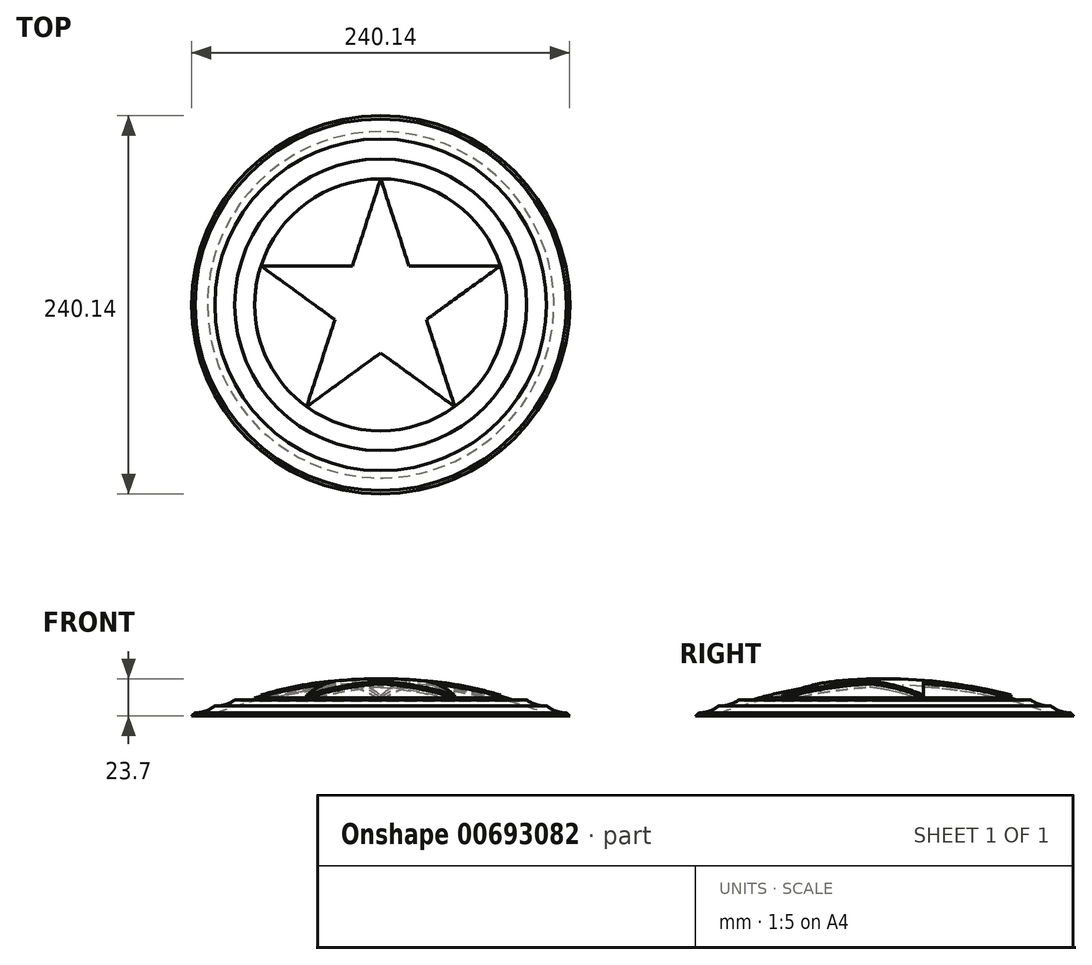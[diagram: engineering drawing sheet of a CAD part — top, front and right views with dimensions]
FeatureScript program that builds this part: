
annotation { "Feature Type Name" : "Feature", "Feature Type Description" : "" }
export const myFeature = defineFeature(function(context is Context, id is Id, definition is map)
    precondition{}
    {
        {
            var Q0;
            Q0=qCreatedBy(makeId("Front.planeOp"),FACE);
            var sketch = newSketch(context, id + "F0", { "sketchPlane" : qUnion([Q0])});
            skPoint(sketch, "E0", {"position": v(0, 111.23) * mm});
            skLineSegment(sketch, "E1", {"start": v(0, 111.23) * mm, "end": v(0, 131.23) * mm});
            skPoint(sketch, "E2.orphan", {"position": v(-118, 111.23) * mm});
            skPoint(sketch, "E3", {"position": v(0, -180.77) * mm});
            skPoint(sketch, "E4", {"position": v(118, 141.23) * mm});
            skPoint(sketch, "E5", {"position": v(0, 141.23) * mm});
            skLineSegment(sketch, "E6", {"start": v(118, 141.23) * mm, "end": v(105.33, 141.23) * mm, "construction": true});
            skLineSegment(sketch, "E7", {"start": v(105.33, 141.23) * mm, "end": v(92.67, 141.23) * mm, "construction": true});
            skLineSegment(sketch, "E8", {"start": v(92.67, 141.23) * mm, "end": v(80, 141.23) * mm, "construction": true});
            skLineSegment(sketch, "E9", {"start": v(80, 141.23) * mm, "end": v(0, 141.23) * mm, "construction": true});
            skPoint(sketch, "E10", {"position": v(80, 120.8) * mm});
            skPoint(sketch, "E11", {"position": v(92.67, 119.52) * mm});
            skPoint(sketch, "E12", {"position": v(105.33, 141.23) * mm});
            skPoint(sketch, "E13", {"position": v(105.33, 115.67) * mm});
            skArc(sketch, "E14", {"start": v(80, 120.8) * mm, "mid": v(86.23, 119.14) * mm, "end": v(92.67, 119.52) * mm});
            skPoint(sketch, "E15", {"position": v(86.23, 119.14) * mm});
            skArc(sketch, "E16", {"start": v(92.67, 119.52) * mm, "mid": v(98.68, 116.53) * mm, "end": v(105.33, 115.67) * mm});
            skArc(sketch, "E17", {"start": v(105.33, 115.67) * mm, "mid": v(111.29, 112.37) * mm, "end": v(118, 111.23) * mm});
            skPoint(sketch, "E18", {"position": v(98.68, 116.53) * mm});
            skPoint(sketch, "E19", {"position": v(111.29, 112.37) * mm});
            skLineSegment(sketch, "E20", {"start": v(86.23, 119.14) * mm, "end": v(88.27, 139.32) * mm, "construction": true});
            skLineSegment(sketch, "E21", {"start": v(98.68, 116.53) * mm, "end": v(104.57, 135.94) * mm, "construction": true});
            skLineSegment(sketch, "E22", {"start": v(111.29, 112.37) * mm, "end": v(118, 131.52) * mm, "construction": true});
            skArc(sketch, "E23", {"start": v(118, 111.23) * mm, "mid": v(119.12, 110.32) * mm, "end": v(120.07, 109.23) * mm});
            skLineSegment(sketch, "E24", {"start": v(120.07, 109.23) * mm, "end": v(0, 109.23) * mm});
            skLineSegment(sketch, "E25", {"start": v(0, 111.23) * mm, "end": v(0, 109.23) * mm});
            skArc(sketch, "E26.trimOffspring", {"start": v(80, 120.8) * mm, "mid": v(40.34, 128.61) * mm, "end": v(0, 131.23) * mm});
            skSolve(sketch);
        }
        {
            var Q0;
            Q0=makeQuery(id+"F0.imprint","IMPRINT",FACE,{"disambiguationData":[TD([[makeQuery(id+"F0.imprint","IMPRINT",EDGE,{"derivedFrom":sQuery(id+"F0.wireOp",EDGE,"E1")}),-1.0]])]});
            var Q1;
            Q1=sQuery(id+"F0.wireOp",EDGE,"E1");
            revolve(context, id + "F1", {"entities" : qUnion([Q0]), "axis" : qUnion([Q1]), "revolveType" : RevolveType.FULL});
        }
        {
            var Q0;
            Q0=qCreatedBy(makeId("Front.planeOp"),FACE);
            var sketch = newSketch(context, id + "F2", { "sketchPlane" : qUnion([Q0])});
            skLineSegment(sketch, "E27", {"start": v(0, 13.93) * mm, "end": v(0, 24.77) * mm, "construction": true});
            skLineSegment(sketch, "E28", {"start": v(0, 13.93) * mm, "end": v(-109.96, 13.93) * mm, "construction": true});
            skPoint(sketch, "E29", {"position": v(-120.4, 109.23) * mm});
            skPoint(sketch, "E30", {"position": v(-80, 13.93) * mm});
            skArc(sketch, "E31", {"start": v(0, 37.93) * mm, "mid": v(-61.38, 31.87) * mm, "end": v(-120.4, 13.93) * mm});
            skArc(sketch, "E32", {"start": v(-11.3, 33.88) * mm, "mid": v(-61.44, 27.93) * mm, "end": v(-109.96, 13.93) * mm});
            skLineSegment(sketch, "E33", {"start": v(-109.96, 13.93) * mm, "end": v(-120.4, 13.93) * mm});
            skLineSegment(sketch, "E34", {"start": v(0, 24.77) * mm, "end": v(0, 37.93) * mm});
            skLineSegment(sketch, "E35", {"start": v(-11.3, 33.88) * mm, "end": v(0, 34.29) * mm});
            skSolve(sketch);
        }
        {
            var Q0;
            Q0=makeQuery(id+"F2.imprint","IMPRINT",FACE,{"disambiguationData":[TD([[makeQuery(id+"F2.imprint","IMPRINT",EDGE,{"derivedFrom":sQuery(id+"F2.wireOp",EDGE,"E31")}),1.0]])]});
            var Q1;
            Q1=sQuery(id+"F2.wireOp",EDGE,"E34");
            revolve(context, id + "F3", {"entities" : qUnion([Q0]), "axis" : qUnion([Q1]), "revolveType" : RevolveType.FULL});
        }
        {
            var Q0;
            Q0=makeQuery(id+"F3.opRevolve","SWEPT_FACE",FACE,{"disambiguationData":[OSD([sQuery(id+"F2.wireOp",EDGE,"E33")])]});
            var sketch = newSketch(context, id + "F4", { "sketchPlane" : qUnion([Q0])});
            skPoint(sketch, "E36", {"position": v(0, 0) * mm});
            skCircle(sketch, "E37.cCircle", {"center": v(0, 0) * mm, "radius": 64.72 * mm, "construction": true});
            skLineSegment(sketch, "E37.0", {"start": v(0, -80) * mm, "end": v(-76.08, -24.72) * mm, "construction": true});
            skLineSegment(sketch, "E37.1", {"start": v(-76.08, -24.72) * mm, "end": v(-47.02, 64.72) * mm, "construction": true});
            skLineSegment(sketch, "E37.2", {"start": v(-47.02, 64.72) * mm, "end": v(47.02, 64.72) * mm, "construction": true});
            skLineSegment(sketch, "E37.3", {"start": v(47.02, 64.72) * mm, "end": v(76.08, -24.72) * mm, "construction": true});
            skLineSegment(sketch, "E37.4", {"start": v(76.08, -24.72) * mm, "end": v(0, -80) * mm, "construction": true});
            skPoint(sketch, "E37.0.midPoint", {"position": v(-38.04, -52.36) * mm});
            skLineSegment(sketch, "E38", {"start": v(76.08, -24.72) * mm, "end": v(17.96, -24.72) * mm});
            skLineSegment(sketch, "E39", {"start": v(0, -80) * mm, "end": v(17.96, -24.72) * mm});
            skLineSegment(sketch, "E40", {"start": v(-47.02, 64.72) * mm, "end": v(-29.06, 9.44) * mm});
            skLineSegment(sketch, "E41", {"start": v(76.08, -24.72) * mm, "end": v(29.06, 9.44) * mm});
            skLineSegment(sketch, "E42", {"start": v(-76.08, -24.72) * mm, "end": v(-29.06, 9.44) * mm});
            skLineSegment(sketch, "E43", {"start": v(0, 0) * mm, "end": v(0, -80) * mm, "construction": true});
            skLineSegment(sketch, "E44.trimOffspring", {"start": v(29.06, 9.44) * mm, "end": v(47.02, 64.72) * mm});
            skLineSegment(sketch, "E45.trimOffspring", {"start": v(-17.96, -24.72) * mm, "end": v(-76.08, -24.72) * mm});
            skLineSegment(sketch, "E46.trimOffspring", {"start": v(-17.96, -24.72) * mm, "end": v(0, -80) * mm});
            skLineSegment(sketch, "E47.trimOffspring", {"start": v(0, 30.56) * mm, "end": v(47.02, 64.72) * mm});
            skLineSegment(sketch, "E48.trimOffspring", {"start": v(0, 30.56) * mm, "end": v(-47.02, 64.72) * mm});
            skSolve(sketch);
        }
        {
            var Q0;
            Q0=makeQuery(id+"F4.imprint","IMPRINT",FACE,{"disambiguationData":[TD([[makeQuery(id+"F4.imprint","IMPRINT",EDGE,{"derivedFrom":sQuery(id+"F4.wireOp",EDGE,"E38")}),1.0]])]});
            var Q1;
            {var subQ0=sQuery(id+"F2.wireOp",EDGE,"E33");Q1=makeQuery(id+"F4.imprint","IMPRINT",FACE,{"disambiguationData":[TD([[makeQuery(id+"F4.imprint","IMPRINT",EDGE,{"derivedFrom":makeQuery(id+"F3.opRevolve","SWEPT_EDGE",EDGE,{"disambiguationData":[OSD([sQuery(id+"F2.wireOp",EDGE,"E31"),subQ0])]})}),1.0]])]});}
            var Q2;
            Q2=makeQuery(id+"F3.opRevolve","SWEPT_BODY",BODY,{"disambiguationData":[OSD([sQuery(id+"F2.wireOp",EDGE,"E31"),sQuery(id+"F2.wireOp",EDGE,"E32"),sQuery(id+"F2.wireOp",EDGE,"E33"),sQuery(id+"F2.wireOp",EDGE,"E34")])]});
            extrude(context, id + "F5", {"entities" : qUnion([Q0, Q1]), "operationType" : NewBodyOperationType.REMOVE, "endBound" : BoundingType.UP_TO_BODY, "oppositeDirection" : true, "depth" : 25 * mm, "endBoundEntityBody" : qUnion([Q2]), "offsetDistance" : 25 * mm});
        }
        {
            var Q0;
            Q0=makeQuery(id+"F1.opRevolve","SWEPT_FACE",FACE,{"disambiguationData":[OSD([sQuery(id+"F0.wireOp",EDGE,"E24")])]});
            var sketch = newSketch(context, id + "F6", { "sketchPlane" : qUnion([Q0])});
            skCircle(sketch, "E49.cCircle", {"center": v(0, 0) * mm, "radius": 64.72 * mm, "construction": true});
            skLineSegment(sketch, "E49.0", {"start": v(76.08, -24.72) * mm, "end": v(0, -80) * mm, "construction": true});
            skLineSegment(sketch, "E49.1", {"start": v(0, -80) * mm, "end": v(-76.08, -24.72) * mm, "construction": true});
            skLineSegment(sketch, "E49.2", {"start": v(-76.08, -24.72) * mm, "end": v(-47.02, 64.72) * mm, "construction": true});
            skLineSegment(sketch, "E49.3", {"start": v(-47.02, 64.72) * mm, "end": v(47.02, 64.72) * mm, "construction": true});
            skLineSegment(sketch, "E49.4", {"start": v(47.02, 64.72) * mm, "end": v(76.08, -24.72) * mm, "construction": true});
            skPoint(sketch, "E49.0.midPoint", {"position": v(38.04, -52.36) * mm});
            skLineSegment(sketch, "E50", {"start": v(-47.02, 64.72) * mm, "end": v(-29.06, 9.44) * mm});
            skLineSegment(sketch, "E51", {"start": v(0, -80) * mm, "end": v(17.96, -24.72) * mm});
            skLineSegment(sketch, "E52", {"start": v(47.02, 64.72) * mm, "end": v(0, 30.56) * mm});
            skLineSegment(sketch, "E53", {"start": v(-76.08, -24.72) * mm, "end": v(-17.96, -24.72) * mm});
            skLineSegment(sketch, "E54", {"start": v(76.08, -24.72) * mm, "end": v(29.06, 9.44) * mm});
            skLineSegment(sketch, "E55.trimOffspring", {"start": v(-17.96, -24.72) * mm, "end": v(0, -80) * mm});
            skLineSegment(sketch, "E56.trimOffspring", {"start": v(-29.06, 9.44) * mm, "end": v(-76.08, -24.72) * mm});
            skLineSegment(sketch, "E57.trimOffspring", {"start": v(0, 30.56) * mm, "end": v(-47.02, 64.72) * mm});
            skLineSegment(sketch, "E58.trimOffspring", {"start": v(29.06, 9.44) * mm, "end": v(47.02, 64.72) * mm});
            skLineSegment(sketch, "E59.trimOffspring", {"start": v(17.96, -24.72) * mm, "end": v(76.08, -24.72) * mm});
            skSolve(sketch);
        }
        {
            var Q0;
            Q0=makeQuery(id+"F6.imprint","IMPRINT",FACE,{"disambiguationData":[TD([[makeQuery(id+"F6.imprint","IMPRINT",EDGE,{"derivedFrom":sQuery(id+"F6.wireOp",EDGE,"E50")}),1.0]])]});
            extrude(context, id + "F7", {"entities" : qUnion([Q0]), "operationType" : NewBodyOperationType.REMOVE, "endBound" : BoundingType.UP_TO_NEXT, "oppositeDirection" : true, "depth" : 25 * mm, "offsetDistance" : 25 * mm});
        }
        {
            var Q0;
            Q0=qCreatedBy(makeId("Front.planeOp"),FACE);
            var sketch = newSketch(context, id + "F8", { "sketchPlane" : qUnion([Q0])});
            skPoint(sketch, "E60", {"position": v(0, 109.23) * mm});
            skPoint(sketch, "E61", {"position": v(-110, 109.23) * mm});
            skArc(sketch, "E62", {"start": v(0, 129.4) * mm, "mid": v(-55.92, 124.31) * mm, "end": v(-110, 109.23) * mm});
            skLineSegment(sketch, "E63", {"start": v(-110, 109.23) * mm, "end": v(0, 109.23) * mm});
            skLineSegment(sketch, "E64", {"start": v(0, 129.4) * mm, "end": v(0, 109.23) * mm});
            skSolve(sketch);
        }
        {
            var Q0;
            Q0=makeQuery(id+"F8.imprint","IMPRINT",FACE,{"disambiguationData":[TD([[makeQuery(id+"F8.imprint","IMPRINT",EDGE,{"derivedFrom":sQuery(id+"F8.wireOp",EDGE,"E62")}),1.0]])]});
            var Q1;
            Q1=sQuery(id+"F8.wireOp",EDGE,"E64");
            revolve(context, id + "F9", {"operationType" : NewBodyOperationType.REMOVE, "entities" : qUnion([Q0]), "axis" : qUnion([Q1]), "revolveType" : RevolveType.FULL, "oppositeDirection" : true});
        }
        {
            var Q0;
            Q0=makeQuery(id+"F3.opRevolve","SWEPT_BODY",BODY,{"disambiguationData":[OSD([sQuery(id+"F2.wireOp",EDGE,"E31"),sQuery(id+"F2.wireOp",EDGE,"E32"),sQuery(id+"F2.wireOp",EDGE,"E33"),sQuery(id+"F2.wireOp",EDGE,"E34")])]});
            transform(context, id + "F10", {"entities" : qUnion([Q0]), "transformType" : TransformType.TRANSLATION_3D, "dx" : 0 * mm, "dy" : 0 * mm, "dz" : 95 * mm, "makeCopy" : false});
        }
    });
